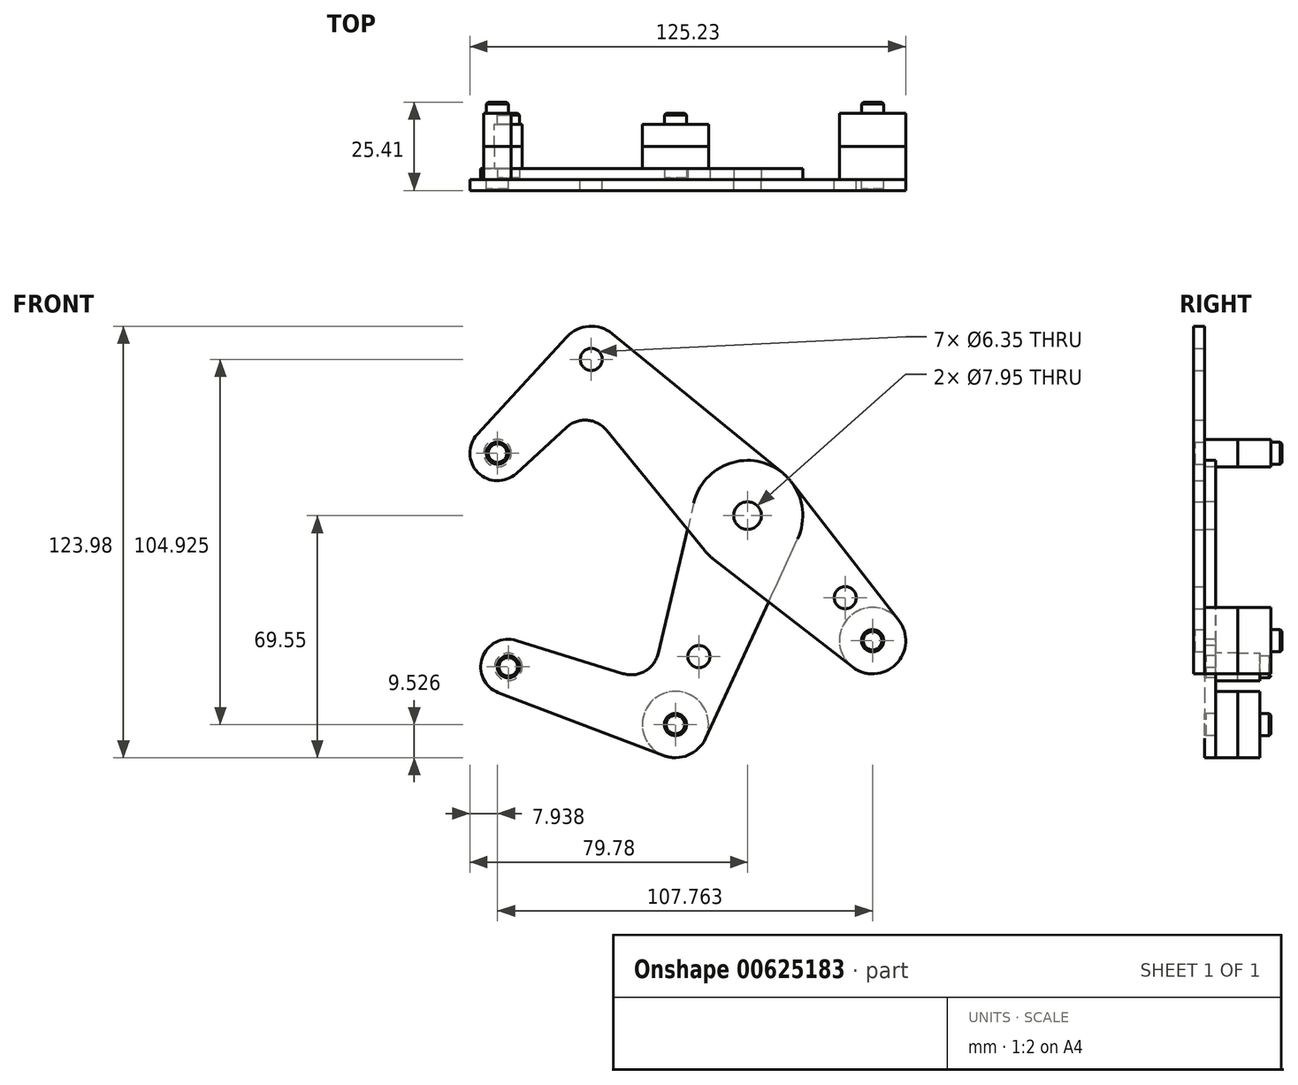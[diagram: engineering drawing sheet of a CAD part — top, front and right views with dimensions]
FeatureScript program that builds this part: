
annotation { "Feature Type Name" : "Feature", "Feature Type Description" : "" }
export const myFeature = defineFeature(function(context is Context, id is Id, definition is map)
    precondition{}
    {
        {
            var Q0;
            Q0=qCreatedBy(makeId("Front.planeOp"),FACE);
            var sketch = newSketch(context, id + "F0", { "sketchPlane" : qUnion([Q0])});
            skCircle(sketch, "E0", {"center": v(0, 0) * mm, "radius": 3.98 * mm});
            skCircle(sketch, "E1", {"center": v(0, 0) * mm, "radius": 15.88 * mm});
            skLineSegment(sketch, "E2", {"start": v(-44.9, 44.9) * mm, "end": v(35.92, -35.92) * mm, "construction": true});
            skCircle(sketch, "E3", {"center": v(35.92, -35.92) * mm, "radius": 3.18 * mm});
            skCircle(sketch, "E4", {"center": v(35.92, -35.92) * mm, "radius": 9.53 * mm});
            skCircle(sketch, "E5", {"center": v(-44.9, 44.9) * mm, "radius": 3.18 * mm});
            skCircle(sketch, "E6", {"center": v(-44.9, 44.9) * mm, "radius": 9.53 * mm});
            skCircle(sketch, "E7", {"center": v(0, 0) * mm, "radius": 3.18 * mm});
            skCircle(sketch, "E8", {"center": v(28.07, -23.58) * mm, "radius": 3.18 * mm});
            skLineSegment(sketch, "E9", {"start": v(-44.9, 44.9) * mm, "end": v(-71.84, 17.96) * mm, "construction": true});
            skCircle(sketch, "E10", {"center": v(-71.84, 17.96) * mm, "radius": 3.18 * mm});
            skCircle(sketch, "E11", {"center": v(-71.84, 17.96) * mm, "radius": 7.94 * mm});
            skPoint(sketch, "E12", {"position": v(25.83, -25.83) * mm});
            skLineSegment(sketch, "E13", {"start": v(-9.73, -12.54) * mm, "end": v(30.08, -43.45) * mm});
            skLineSegment(sketch, "E14", {"start": v(12.54, 9.73) * mm, "end": v(43.45, -30.08) * mm});
            skLineSegment(sketch, "E15", {"start": v(-77.68, 23.33) * mm, "end": v(-51.91, 51.35) * mm});
            skLineSegment(sketch, "E16", {"start": v(-38.87, 52.28) * mm, "end": v(10.05, 12.3) * mm});
            skLineSegment(sketch, "E17", {"start": v(-66.47, 12.12) * mm, "end": v(-52.09, 25.35) * mm});
            skLineSegment(sketch, "E18", {"start": v(-12.3, -10.05) * mm, "end": v(-40.55, 24.53) * mm});
            skArc(sketch, "E19", {"start": v(-52.09, 25.35) * mm, "mid": v(-46.14, 27.43) * mm, "end": v(-40.55, 24.53) * mm});
            skLineSegment(sketch, "E20", {"start": v(0, 0) * mm, "end": v(-20.72, -60.02) * mm, "construction": true});
            skLineSegment(sketch, "E21", {"start": v(-20.72, -60.02) * mm, "end": v(-68.74, -43.45) * mm, "construction": true});
            skCircle(sketch, "E22", {"center": v(-13.98, -40.5) * mm, "radius": 3.18 * mm});
            skCircle(sketch, "E23", {"center": v(-20.72, -60.02) * mm, "radius": 3.18 * mm});
            skCircle(sketch, "E24", {"center": v(-20.72, -60.02) * mm, "radius": 9.53 * mm});
            skCircle(sketch, "E25", {"center": v(-68.74, -43.45) * mm, "radius": 3.18 * mm});
            skCircle(sketch, "E26", {"center": v(-68.74, -43.45) * mm, "radius": 7.94 * mm});
            skLineSegment(sketch, "E27", {"start": v(-71.57, -50.86) * mm, "end": v(-24.11, -68.93) * mm});
            skLineSegment(sketch, "E28", {"start": v(-12.08, -64.02) * mm, "end": v(14.41, -6.66) * mm});
            skLineSegment(sketch, "E29", {"start": v(-66.39, -35.87) * mm, "end": v(-35.78, -45.37) * mm});
            skLineSegment(sketch, "E30", {"start": v(-15.45, 3.65) * mm, "end": v(-25.68, -39.61) * mm});
            skArc(sketch, "E31", {"start": v(-35.78, -45.37) * mm, "mid": v(-29.48, -44.69) * mm, "end": v(-25.68, -39.61) * mm});
            skSolve(sketch);
        }
        {
            var Q0;
            Q0=qCreatedBy(makeId("Front.planeOp"),FACE);
            cPlane(context, id + "F1", {"entities" : qUnion([Q0]), "cplaneType" : CPlaneType.OFFSET, "offset" : 9.52 * mm, "oppositeDirection" : true, "width" : 152.4 * mm, "height" : 152.4 * mm});
        }
        {
            var Q0;
            Q0=makeQuery(id+"F0.imprint","IMPRINT",FACE,{"disambiguationData":[TD([[makeQuery(id+"F0.imprint","IMPRINT",EDGE,{"derivedFrom":sQuery(id+"F0.wireOp",EDGE,"E3")}),-1.0]])]});
            var Q1;
            Q1=makeQuery(id+"F0.imprint","IMPRINT",FACE,{"disambiguationData":[TD([[makeQuery(id+"F0.imprint","IMPRINT",EDGE,{"derivedFrom":sQuery(id+"F0.wireOp",EDGE,"E5")}),-1.0]])]});
            var Q2;
            Q2=makeQuery(id+"F0.imprint","IMPRINT",FACE,{"disambiguationData":[TD([[makeQuery(id+"F0.imprint","IMPRINT",EDGE,{"derivedFrom":sQuery(id+"F0.wireOp",EDGE,"E10")}),-1.0]])]});
            var Q3;
            {var subQ0=sQuery(id+"F0.wireOp",EDGE,"E18");var subQ1=sQuery(id+"F0.wireOp",EDGE,"E1");var subQ2=makeQuery(id+"F0.imprint","INTERSECT",VERTEX,{"derivedFrom":[subQ1,subQ0]});Q3=makeQuery(id+"F0.imprint","IMPRINT",FACE,{"disambiguationData":[TD([[makeQuery(id+"F0.imprint","IMPRINT",EDGE,{"disambiguationData":[TD([[subQ2,1.0]])],"derivedFrom":subQ1}),-1.0]])]});}
            var Q4;
            {var subQ0=sQuery(id+"F0.wireOp",EDGE,"E13");var subQ1=sQuery(id+"F0.wireOp",EDGE,"E1");var subQ2=makeQuery(id+"F0.imprint","INTERSECT",VERTEX,{"derivedFrom":[subQ1,subQ0]});Q4=makeQuery(id+"F0.imprint","IMPRINT",FACE,{"disambiguationData":[TD([[makeQuery(id+"F0.imprint","IMPRINT",EDGE,{"disambiguationData":[TD([[subQ2,-1.0]])],"derivedFrom":subQ1}),-1.0]])]});}
            var Q5;
            {var subQ0=sQuery(id+"F0.wireOp",EDGE,"E15");Q5=makeQuery(id+"F0.imprint","IMPRINT",FACE,{"disambiguationData":[TD([[makeQuery(id+"F0.imprint","IMPRINT",EDGE,{"derivedFrom":subQ0}),-1.0]])]});}
            var Q6;
            Q6=makeQuery(id+"F0.imprint","IMPRINT",FACE,{"disambiguationData":[TD([[makeQuery(id+"F0.imprint","IMPRINT",EDGE,{"derivedFrom":sQuery(id+"F0.wireOp",EDGE,"E8")}),-1.0]])]});
            var Q7;
            Q7=makeQuery(id+"F0.imprint","IMPRINT",FACE,{"disambiguationData":[TD([[makeQuery(id+"F0.imprint","IMPRINT",EDGE,{"derivedFrom":sQuery(id+"F0.wireOp",EDGE,"E0")}),-1.0]])]});
            extrude(context, id + "F2", {"entities" : qUnion([Q0, Q1, Q2, Q3, Q4, Q5, Q6, Q7]), "depth" : 3.17 * mm, "offsetDistance" : 25.4 * mm});
        }
        {
            var Q0;
            Q0=makeQuery(id+"F0.imprint","IMPRINT",FACE,{"disambiguationData":[TD([[makeQuery(id+"F0.imprint","IMPRINT",EDGE,{"derivedFrom":sQuery(id+"F0.wireOp",EDGE,"E25")}),-1.0]])]});
            var Q1;
            Q1=makeQuery(id+"F0.imprint","IMPRINT",FACE,{"disambiguationData":[TD([[makeQuery(id+"F0.imprint","IMPRINT",EDGE,{"derivedFrom":sQuery(id+"F0.wireOp",EDGE,"E0")}),-1.0]])]});
            var Q2;
            Q2=makeQuery(id+"F0.imprint","IMPRINT",FACE,{"disambiguationData":[TD([[makeQuery(id+"F0.imprint","IMPRINT",EDGE,{"derivedFrom":sQuery(id+"F0.wireOp",EDGE,"E23")}),-1.0]])]});
            var Q3;
            {var subQ0=sQuery(id+"F0.wireOp",EDGE,"E13");var subQ1=sQuery(id+"F0.wireOp",EDGE,"E1");var subQ2=makeQuery(id+"F0.imprint","INTERSECT",VERTEX,{"derivedFrom":[subQ1,subQ0]});Q3=makeQuery(id+"F0.imprint","IMPRINT",FACE,{"disambiguationData":[TD([[makeQuery(id+"F0.imprint","IMPRINT",EDGE,{"disambiguationData":[TD([[subQ2,-1.0]])],"derivedFrom":subQ1}),-1.0]])]});}
            var Q4;
            Q4=makeQuery(id+"F0.imprint","IMPRINT",FACE,{"disambiguationData":[TD([[makeQuery(id+"F0.imprint","IMPRINT",EDGE,{"derivedFrom":sQuery(id+"F0.wireOp",EDGE,"E22")}),-1.0]])]});
            var Q5;
            {var subQ0=sQuery(id+"F0.wireOp",EDGE,"E18");var subQ1=sQuery(id+"F0.wireOp",EDGE,"E1");var subQ2=makeQuery(id+"F0.imprint","INTERSECT",VERTEX,{"derivedFrom":[subQ1,subQ0]});Q5=makeQuery(id+"F0.imprint","IMPRINT",FACE,{"disambiguationData":[TD([[makeQuery(id+"F0.imprint","IMPRINT",EDGE,{"disambiguationData":[TD([[subQ2,1.0]])],"derivedFrom":subQ1}),-1.0]])]});}
            extrude(context, id + "F3", {"entities" : qUnion([Q0, Q1, Q2, Q3, Q4, Q5]), "oppositeDirection" : true, "depth" : 3.17 * mm, "offsetDistance" : 25.4 * mm});
        }
        {
            var Q0;
            Q0=makeQuery(id+"F2.opExtrude","CAP_FACE",FACE,{"disambiguationData":[OSD([sQuery(id+"F0.wireOp",EDGE,"E0"),sQuery(id+"F0.wireOp",EDGE,"E1"),sQuery(id+"F0.wireOp",EDGE,"E3"),sQuery(id+"F0.wireOp",EDGE,"E4"),sQuery(id+"F0.wireOp",EDGE,"E5"),sQuery(id+"F0.wireOp",EDGE,"E6"),sQuery(id+"F0.wireOp",EDGE,"E8"),sQuery(id+"F0.wireOp",EDGE,"E10"),sQuery(id+"F0.wireOp",EDGE,"E11"),sQuery(id+"F0.wireOp",EDGE,"E13"),sQuery(id+"F0.wireOp",EDGE,"E14"),sQuery(id+"F0.wireOp",EDGE,"E15"),sQuery(id+"F0.wireOp",EDGE,"E16"),sQuery(id+"F0.wireOp",EDGE,"E17"),sQuery(id+"F0.wireOp",EDGE,"E18"),sQuery(id+"F0.wireOp",EDGE,"E19")])],"isStart":false});
            var sketch = newSketch(context, id + "F4", { "sketchPlane" : qUnion([Q0])});
            skCircle(sketch, "E32", {"center": v(-71.84, 17.96) * mm, "radius": 3.97 * mm});
            skCircle(sketch, "E33", {"center": v(35.92, -35.92) * mm, "radius": 9.53 * mm});
            skSolve(sketch);
        }
        {
            var Q0;
            Q0=makeQuery(id+"F3.opExtrude","CAP_FACE",FACE,{"disambiguationData":[OSD([sQuery(id+"F0.wireOp",EDGE,"E0"),sQuery(id+"F0.wireOp",EDGE,"E1"),sQuery(id+"F0.wireOp",EDGE,"E22"),sQuery(id+"F0.wireOp",EDGE,"E23"),sQuery(id+"F0.wireOp",EDGE,"E24"),sQuery(id+"F0.wireOp",EDGE,"E25"),sQuery(id+"F0.wireOp",EDGE,"E26"),sQuery(id+"F0.wireOp",EDGE,"E27"),sQuery(id+"F0.wireOp",EDGE,"E28"),sQuery(id+"F0.wireOp",EDGE,"E29"),sQuery(id+"F0.wireOp",EDGE,"E30"),sQuery(id+"F0.wireOp",EDGE,"E31")])],"isStart":true});
            var sketch = newSketch(context, id + "F5", { "sketchPlane" : qUnion([Q0])});
            skCircle(sketch, "E34", {"center": v(-20.72, -60.02) * mm, "radius": 9.53 * mm});
            skCircle(sketch, "E35", {"center": v(-68.74, -43.45) * mm, "radius": 3.97 * mm});
            skSolve(sketch);
        }
        {
            var Q0;
            Q0 = qSketchRegion(id + "F4", true);
            var Q1;
            Q1 = qSketchRegion(id + "F5", true);
            var Q2;
            Q2=qCreatedBy(id+"F1.planeOp",FACE);
            extrude(context, id + "F6", {"entities" : qUnion([Q0, Q1]), "endBound" : BoundingType.UP_TO_SURFACE, "oppositeDirection" : true, "depth" : 25.4 * mm, "endBoundEntityFace" : qUnion([Q2]), "offsetDistance" : 25.4 * mm});
        }
        {
            var Q0;
            Q0=makeQuery(id+"F2.opExtrude","SWEPT_BODY",BODY,{"disambiguationData":[OSD([sQuery(id+"F0.wireOp",EDGE,"E0"),sQuery(id+"F0.wireOp",EDGE,"E1"),sQuery(id+"F0.wireOp",EDGE,"E3"),sQuery(id+"F0.wireOp",EDGE,"E4"),sQuery(id+"F0.wireOp",EDGE,"E5"),sQuery(id+"F0.wireOp",EDGE,"E6"),sQuery(id+"F0.wireOp",EDGE,"E8"),sQuery(id+"F0.wireOp",EDGE,"E10"),sQuery(id+"F0.wireOp",EDGE,"E11"),sQuery(id+"F0.wireOp",EDGE,"E13"),sQuery(id+"F0.wireOp",EDGE,"E14"),sQuery(id+"F0.wireOp",EDGE,"E15"),sQuery(id+"F0.wireOp",EDGE,"E16"),sQuery(id+"F0.wireOp",EDGE,"E17"),sQuery(id+"F0.wireOp",EDGE,"E18"),sQuery(id+"F0.wireOp",EDGE,"E19")])]});
            var Q1;
            Q1=makeQuery(id+"F3.opExtrude","SWEPT_BODY",BODY,{"disambiguationData":[OSD([sQuery(id+"F0.wireOp",EDGE,"E0"),sQuery(id+"F0.wireOp",EDGE,"E1"),sQuery(id+"F0.wireOp",EDGE,"E22"),sQuery(id+"F0.wireOp",EDGE,"E23"),sQuery(id+"F0.wireOp",EDGE,"E24"),sQuery(id+"F0.wireOp",EDGE,"E25"),sQuery(id+"F0.wireOp",EDGE,"E26"),sQuery(id+"F0.wireOp",EDGE,"E27"),sQuery(id+"F0.wireOp",EDGE,"E28"),sQuery(id+"F0.wireOp",EDGE,"E29"),sQuery(id+"F0.wireOp",EDGE,"E30"),sQuery(id+"F0.wireOp",EDGE,"E31")])]});
            var Q2;
            Q2=makeQuery(id+"F6.opExtrude","SWEPT_BODY",BODY,{"disambiguationData":[OSD([sQuery(id+"F4.wireOp",EDGE,"E32")])]});
            var Q3;
            Q3=makeQuery(id+"F6.opExtrude","SWEPT_BODY",BODY,{"disambiguationData":[OSD([sQuery(id+"F4.wireOp",EDGE,"E33")])]});
            var Q4;
            Q4=makeQuery(id+"F6.opExtrude","SWEPT_BODY",BODY,{"disambiguationData":[OSD([sQuery(id+"F5.wireOp",EDGE,"E34")])]});
            var Q5;
            Q5=makeQuery(id+"F6.opExtrude","SWEPT_BODY",BODY,{"disambiguationData":[OSD([sQuery(id+"F5.wireOp",EDGE,"E35")])]});
            booleanBodies(context, id + "F7", {"operationType" : BooleanOperationType.SUBTRACTION, "tools" : qUnion([Q0, Q1]), "targets" : qUnion([Q2, Q3, Q4, Q5]), "keepTools" : true});
        }
        {
            var Q0;
            Q0=makeQuery(id+"F6.opExtrude","CAP_FACE",FACE,{"disambiguationData":[OSD([sQuery(id+"F4.wireOp",EDGE,"E32")])],"isStart":true});
            var Q1;
            Q1=makeQuery(id+"F6.opExtrude","CAP_FACE",FACE,{"disambiguationData":[OSD([sQuery(id+"F5.wireOp",EDGE,"E35")])],"isStart":true});
            var Q2;
            Q2=makeQuery(id+"F6.opExtrude","CAP_FACE",FACE,{"disambiguationData":[OSD([sQuery(id+"F5.wireOp",EDGE,"E34")])],"isStart":true});
            var Q3;
            Q3=makeQuery(id+"F6.opExtrude","CAP_FACE",FACE,{"disambiguationData":[OSD([sQuery(id+"F4.wireOp",EDGE,"E33")])],"isStart":true});
            chamfer(context, id + "F8", {"entities" : qUnion([Q0, Q1, Q2, Q3]), "width" : 0.5 * mm, "tangentPropagation" : true});
        }
        {
            var Q0;
            Q0=makeQuery(id+"F6.opExtrude","SWEPT_BODY",BODY,{"disambiguationData":[OSD([sQuery(id+"F4.wireOp",EDGE,"E33")])]});
            var Q1;
            Q1=makeQuery(id+"F6.opExtrude","SWEPT_BODY",BODY,{"disambiguationData":[OSD([sQuery(id+"F4.wireOp",EDGE,"E32")])]});
            var Q2;
            Q2=makeQuery(id+"F6.opExtrude","SWEPT_BODY",BODY,{"disambiguationData":[OSD([sQuery(id+"F5.wireOp",EDGE,"E34")])]});
            var Q3;
            Q3=makeQuery(id+"F6.opExtrude","SWEPT_BODY",BODY,{"disambiguationData":[OSD([sQuery(id+"F5.wireOp",EDGE,"E35")])]});
            var Q4;
            Q4=qCreatedBy(id+"F1.planeOp",FACE);
            mirror(context, id + "F9", {"entities" : qUnion([Q0, Q1, Q2, Q3]), "mirrorPlane" : qUnion([Q4])});
        }
    });
